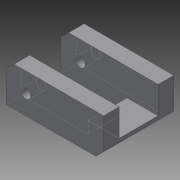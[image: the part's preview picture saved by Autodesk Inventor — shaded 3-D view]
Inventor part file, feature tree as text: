
AUTODESK INVENTOR PART (.ipt)
format: ipt  version: 2015 (Build 190159000, 159)  size: 109,056 bytes
history: native  units: mm
features: extrude x3, sketch x3, chamfer x2
ambient origin geometry x8: Origin, YZ Plane, XZ Plane, XY Plane, X Axis, Y Axis, Z Axis, Center Point
bodies: Solid1 (feature_tree)
feature tree (8):
  extrude  "Extrusion1"  Depth=4.0mm
  extrude  "Extrusion2"  Depth=25.0mm
  extrude  "Extrusion3"  Depth=10.0mm TaperAngle=0.0deg
  chamfer  "Chamfer1"  Distance=8.0mm
  chamfer  "Chamfer2"  Distance=3.0mm
  sketch  "Sketch1"  dims[d0=4.0mm d1=4.0mm]
  sketch  "Sketch2"  dims[d2=10.0mm d3=25.0mm]
  sketch  "Sketch3"  dims[d4=25.0mm d5=10.0mm d6=0.0mm d7=8.0mm d8=3.0mm d9=0.0mm d10=5.0mm d11=2.5mm d12=30.0mm d13=0.0mm d14=2.0mm d15=2.0mm d16=45.0deg d17=2.0mm d18=2.0mm d19=45.0deg]
